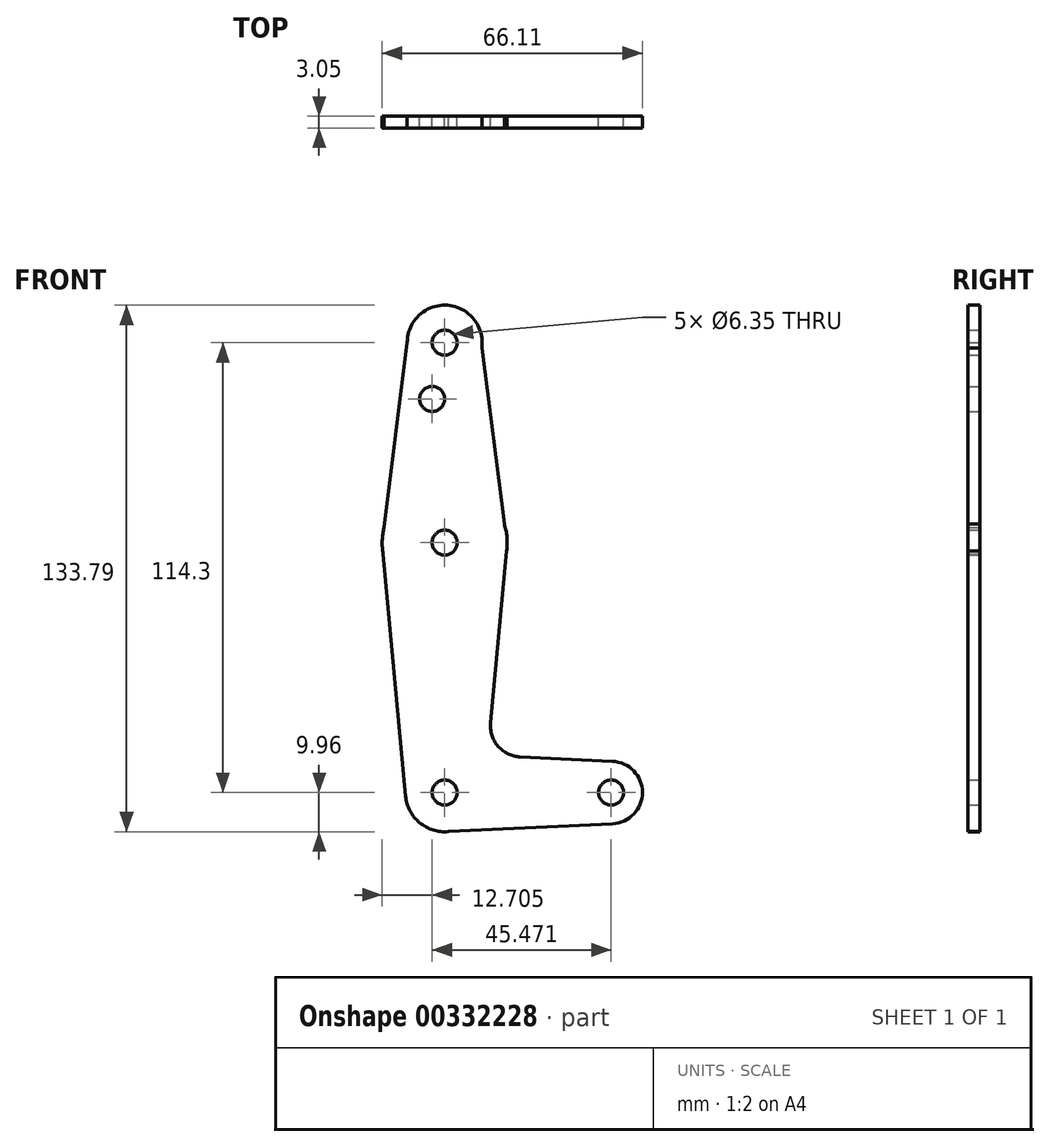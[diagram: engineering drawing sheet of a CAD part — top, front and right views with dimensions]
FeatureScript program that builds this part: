
annotation { "Feature Type Name" : "Feature", "Feature Type Description" : "" }
export const myFeature = defineFeature(function(context is Context, id is Id, definition is map)
    precondition{}
    {
        {
            var Q0;
            Q0=qCreatedBy(makeId("Front.planeOp"),FACE);
            var sketch = newSketch(context, id + "F0", { "sketchPlane" : qUnion([Q0])});
            skLineSegment(sketch, "E0", {"start": v(0, 114.3) * mm, "end": v(0, 0) * mm});
            skCircle(sketch, "E1", {"center": v(0, 114.3) * mm, "radius": 9.53 * mm});
            skCircle(sketch, "E2", {"center": v(0, 0) * mm, "radius": 9.96 * mm});
            skLineSegment(sketch, "E3", {"start": v(0, 0) * mm, "end": v(42.3, 0) * mm});
            skCircle(sketch, "E4", {"center": v(42.3, 0) * mm, "radius": 7.94 * mm});
            skCircle(sketch, "E5", {"center": v(0, 63.5) * mm, "radius": 15.88 * mm});
            skLineSegment(sketch, "E6", {"start": v(8.77, 118.02) * mm, "end": v(15.85, 62.69) * mm});
            skLineSegment(sketch, "E7", {"start": v(-9.52, 114.36) * mm, "end": v(-15.88, 63.5) * mm});
            skLineSegment(sketch, "E8", {"start": v(15.85, 62.69) * mm, "end": v(11.66, 17.73) * mm});
            skLineSegment(sketch, "E9", {"start": v(0, -9.96) * mm, "end": v(42.67, -7.93) * mm});
            skCircle(sketch, "E10", {"center": v(0, 114.3) * mm, "radius": 3.18 * mm});
            skCircle(sketch, "E11", {"center": v(0, 63.5) * mm, "radius": 3.18 * mm});
            skCircle(sketch, "E12", {"center": v(0, 0) * mm, "radius": 3.18 * mm});
            skCircle(sketch, "E13", {"center": v(42.3, 0) * mm, "radius": 3.18 * mm});
            skCircle(sketch, "E14", {"center": v(-3.18, 100.03) * mm, "radius": 3.18 * mm});
            skLineSegment(sketch, "E15", {"start": v(-15.88, 63.5) * mm, "end": v(-9.92, -0.92) * mm});
            skLineSegment(sketch, "E16", {"start": v(19.2, 9.05) * mm, "end": v(42.67, 7.93) * mm});
            skArc(sketch, "E17.filletArc", {"start": v(11.66, 17.73) * mm, "mid": v(13.57, 11.77) * mm, "end": v(19.2, 9.05) * mm});
            skSolve(sketch);
        }
        {
            var Q0;
            Q0 = qSketchRegion(id + "F0", true);
            var Q1;
            {var subQ0=sQuery(id+"F0.wireOp",EDGE,"E2");var subQ1=sQuery(id+"F0.wireOp",EDGE,"E0");var subQ2=makeQuery(id+"F0.imprint","INTERSECT",VERTEX,{"derivedFrom":[subQ1,subQ0]});Q1=makeQuery(id+"F0.imprint","IMPRINT",FACE,{"disambiguationData":[TD([[makeQuery(id+"F0.imprint","IMPRINT",EDGE,{"disambiguationData":[TD([[subQ2,-1.0]])],"derivedFrom":subQ1}),1.0]])]});}
            extrude(context, id + "F1", {"entities" : qUnion([Q0, Q1]), "depth" : 3.05 * mm});
        }
    });
